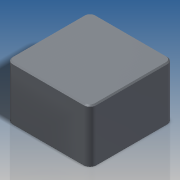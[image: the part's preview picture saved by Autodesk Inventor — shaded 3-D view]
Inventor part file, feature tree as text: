
AUTODESK INVENTOR PART (.ipt)
format: ipt  version: 2016 SP2 (Build 200236200, 236)  size: 109,056 bytes
history: native  units: in
note: dims shown in document units (in); Inventor stores cm internally (conversion verified against a paired STEP export)
features: extrude x1, fillet x1, chamfer x1, sketch x1
ambient origin geometry x8: Origin, YZ Plane, XZ Plane, XY Plane, X Axis, Y Axis, Z Axis, Center Point
bodies: Solid1 (feature_tree)
feature tree (4):
  extrude  "Extrusion1"  Depth=0.2047in TaperAngle=0.0deg
  fillet  "Fillet1"  Radius=0.0236in
  chamfer  "Chamfer1"  Distance=0.0047in Angle=45.0deg
  sketch  "Sketch2"  dims[d0=0.3213in d1=0.2047in d2=0.0in d3=0.0236in d4=0.0047in d5=0.0787in d6=45.0deg]
